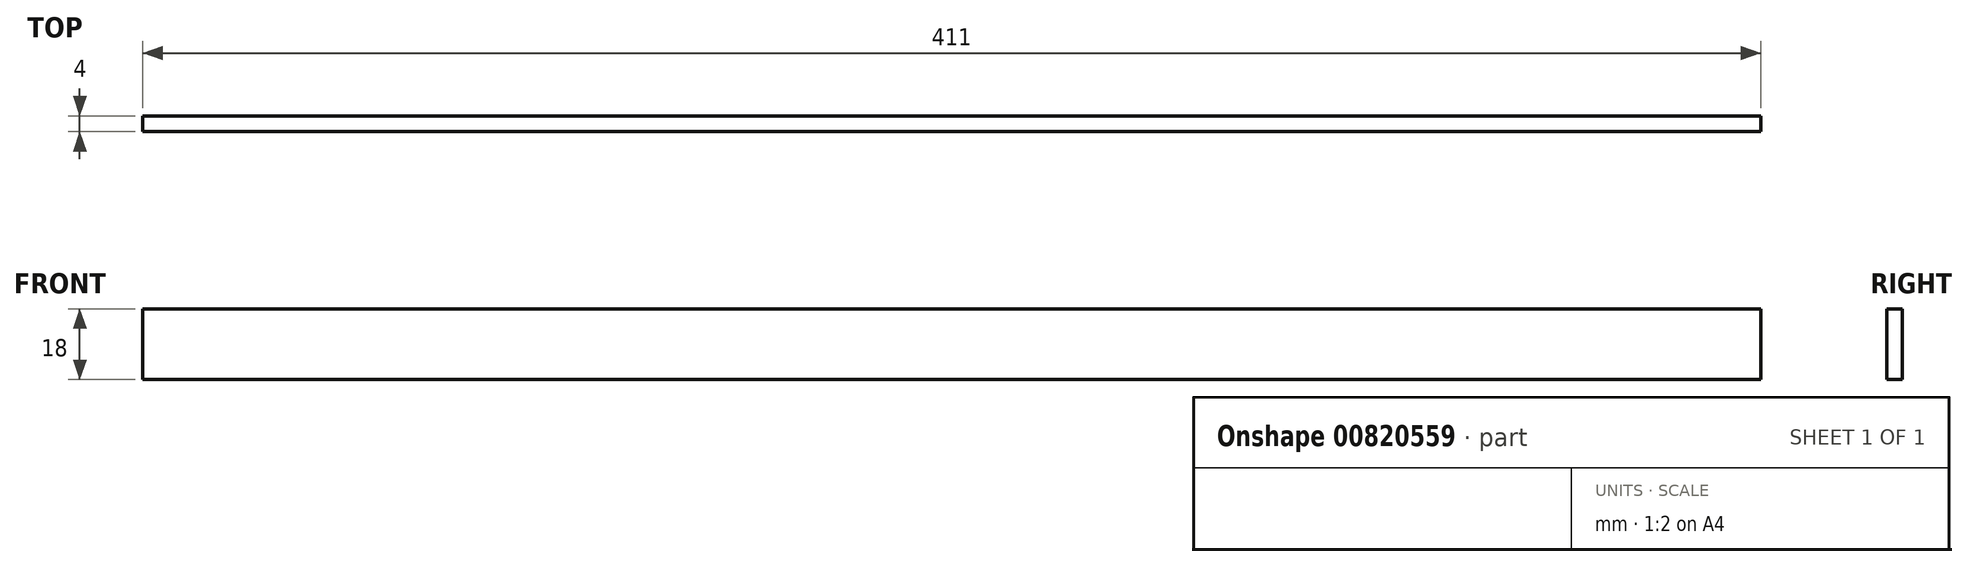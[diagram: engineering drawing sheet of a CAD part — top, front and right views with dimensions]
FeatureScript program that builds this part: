
annotation { "Feature Type Name" : "Feature", "Feature Type Description" : "" }
export const myFeature = defineFeature(function(context is Context, id is Id, definition is map)
    precondition{}
    {
        {
            var Q0;
            Q0=qCreatedBy(makeId("Front.planeOp"),FACE);
            var sketch = newSketch(context, id + "F0", { "sketchPlane" : qUnion([Q0])});
            skLineSegment(sketch, "E0.bottom", {"start": v(205.5, 9) * mm, "end": v(-205.5, 9) * mm});
            skLineSegment(sketch, "E0.top", {"start": v(205.5, -9) * mm, "end": v(-205.5, -9) * mm});
            skLineSegment(sketch, "E0.left", {"start": v(205.5, 9) * mm, "end": v(205.5, -9) * mm});
            skLineSegment(sketch, "E0.right", {"start": v(-205.5, 9) * mm, "end": v(-205.5, -9) * mm});
            skPoint(sketch, "E0.middle", {"position": v(0, 0) * mm});
            skSolve(sketch);
        }
        {
            var Q0;
            Q0=makeQuery(id+"F0.imprint","IMPRINT",FACE,{"disambiguationData":[TD([[makeQuery(id+"F0.imprint","IMPRINT",EDGE,{"derivedFrom":sQuery(id+"F0.wireOp",EDGE,"E0.bottom")}),1.0]])]});
            extrude(context, id + "F1", {"entities" : qUnion([Q0]), "depth" : 4 * mm, "offsetDistance" : 25 * mm});
        }
    });
